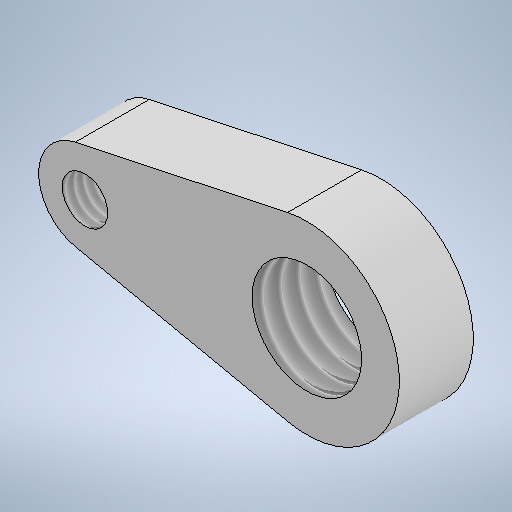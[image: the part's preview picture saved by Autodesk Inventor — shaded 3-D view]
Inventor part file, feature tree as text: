
AUTODESK INVENTOR PART (.ipt)
format: ipt  version: 2025 (Build 290162010, 162A)  size: 274,432 bytes
history: native  units: mm
features: sketch x3, hole x2, extrude x1
ambient origin geometry x8: Origin, YZ Plane, XZ Plane, XY Plane, X Axis, Y Axis, Z Axis, Center Point
bodies: Solid1 (feature_tree)
feature tree (6):
  extrude  "Extrusion1"  Depth=5.0mm
  hole  "Hole2"  [1 undecoded]
  hole  "Hole3"  [1 undecoded]
  sketch  "Sketch1"  dims[d0=2.5mm d1=5.0mm]
  sketch  "Sketch3"  dims[d2=12.0mm d3=4.0mm d4=0.0mm]
  sketch  "Sketch4"  dims[d12=2.459mm d13=6.0mm d14=4.0mm d15=2.0mm d16=90.0deg d17=8.0mm d18=20.594885mm d19=5.917468mm d20=14.0mm d21=4.0mm d22=2.0mm d23=90.0deg d24=8.0mm d25=20.594885mm]
note: 2 required parameter values undecoded (feature->parameter linkage not recoverable at this tier; creation-order binding heuristic only, values carry confidence <= 0.55)
